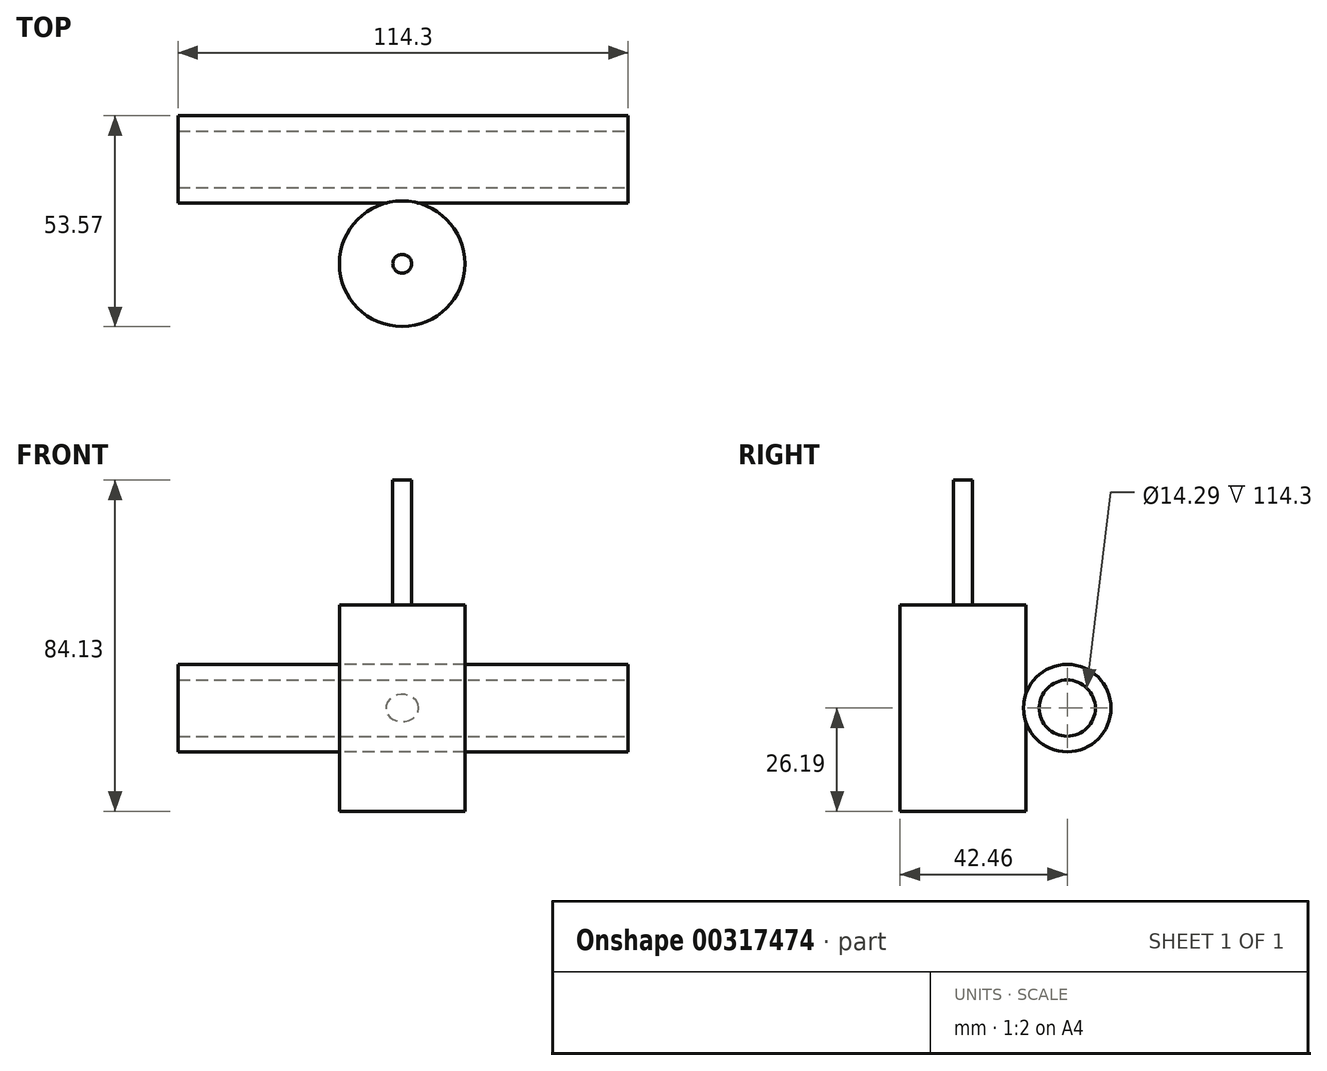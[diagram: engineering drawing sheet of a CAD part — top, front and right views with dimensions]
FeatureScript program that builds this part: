
annotation { "Feature Type Name" : "Feature", "Feature Type Description" : "" }
export const myFeature = defineFeature(function(context is Context, id is Id, definition is map)
    precondition{}
    {
        {
            var Q0;
            Q0=qCreatedBy(makeId("Right.planeOp"),FACE);
            var sketch = newSketch(context, id + "F0", { "sketchPlane" : qUnion([Q0])});
            skCircle(sketch, "E0", {"center": v(0, 0) * mm, "radius": 11.11 * mm});
            skSolve(sketch);
        }
        {
            var Q0;
            Q0=makeQuery(id+"F0.imprint","IMPRINT",FACE,{"disambiguationData":[TD([[makeQuery(id+"F0.imprint","IMPRINT",EDGE,{"derivedFrom":sQuery(id+"F0.wireOp",EDGE,"E0")}),1.0]])]});
            extrude(context, id + "F1", {"entities" : qUnion([Q0]), "endBound" : BoundingType.SYMMETRIC, "depth" : 114.3 * mm});
        }
        {
            var Q0;
            Q0=makeQuery(id+"F1.opExtrude","CAP_FACE",FACE,{"disambiguationData":[OSD([sQuery(id+"F0.wireOp",EDGE,"E0")])],"isStart":false});
            var sketch = newSketch(context, id + "F2", { "sketchPlane" : qUnion([Q0])});
            skSolve(sketch);
        }
        {
            var Q0;
            Q0=makeQuery(id+"F2.imprint","IMPRINT",FACE,{"disambiguationData":[TD([[makeQuery(id+"F2.imprint","IMPRINT",EDGE,{"derivedFrom":makeQuery(id+"F1.opExtrude","CAP_EDGE",EDGE,{"disambiguationData":[OSD([sQuery(id+"F0.wireOp",EDGE,"E0")])],"isStart":false})}),1.0]])]});
            var sketch = newSketch(context, id + "F3", { "sketchPlane" : qUnion([Q0])});
            skCircle(sketch, "E1", {"center": v(0, 0) * mm, "radius": 7.14 * mm});
            skSolve(sketch);
        }
        {
            var Q0;
            Q0 = qSketchRegion(id + "F3", true);
            extrude(context, id + "F4", {"entities" : qUnion([Q0]), "operationType" : NewBodyOperationType.REMOVE, "oppositeDirection" : true, "depth" : 114.3 * mm});
        }
        {
            var Q0;
            Q0=qCreatedBy(makeId("Top.planeOp"),FACE);
            var sketch = newSketch(context, id + "F5", { "sketchPlane" : qUnion([Q0])});
            skCircle(sketch, "E2", {"center": v(-0.23, -26.5) * mm, "radius": 15.95 * mm});
            skSolve(sketch);
        }
        {
            var Q0;
            Q0 = qSketchRegion(id + "F5", true);
            extrude(context, id + "F6", {"entities" : qUnion([Q0]), "operationType" : NewBodyOperationType.ADD, "endBound" : BoundingType.SYMMETRIC, "depth" : 52.4 * mm});
        }
        {
            var Q0;
            Q0=makeQuery(id+"F6.opExtrude","CAP_FACE",FACE,{"disambiguationData":[OSD([sQuery(id+"F5.wireOp",EDGE,"E2")])],"isStart":false});
            var sketch = newSketch(context, id + "F7", { "sketchPlane" : qUnion([Q0])});
            skCircle(sketch, "E3", {"center": v(-0.23, -26.5) * mm, "radius": 2.38 * mm});
            skSolve(sketch);
        }
        {
            var Q0;
            Q0 = qSketchRegion(id + "F7", true);
            extrude(context, id + "F8", {"entities" : qUnion([Q0]), "operationType" : NewBodyOperationType.ADD, "depth" : 31.75 * mm});
        }
    });
